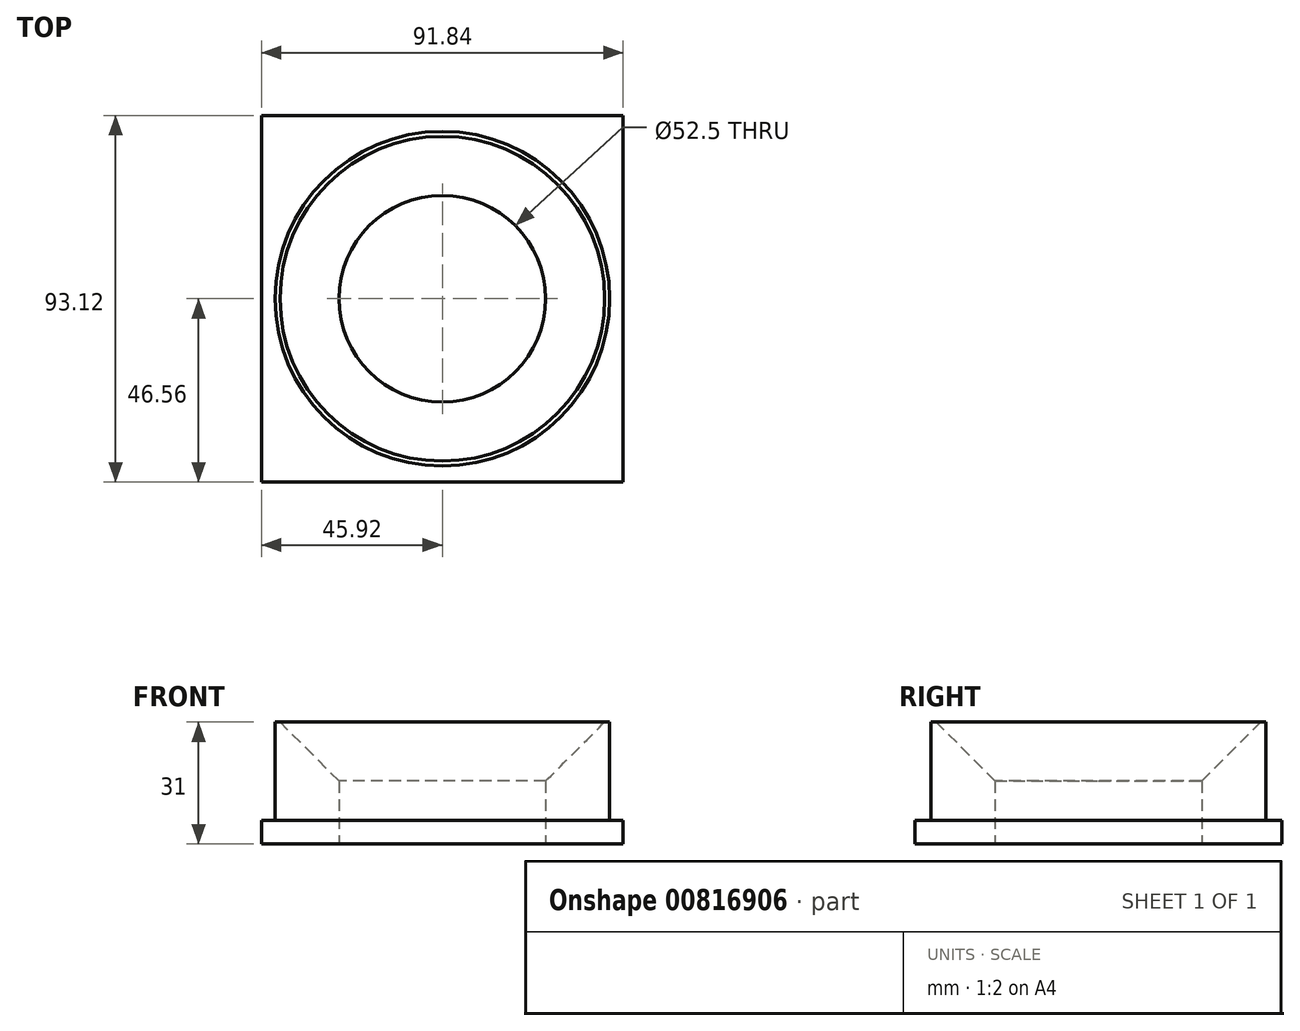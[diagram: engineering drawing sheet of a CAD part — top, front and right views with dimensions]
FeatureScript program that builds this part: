
annotation { "Feature Type Name" : "Feature", "Feature Type Description" : "" }
export const myFeature = defineFeature(function(context is Context, id is Id, definition is map)
    precondition{}
    {
        {
            var Q0;
            Q0=qCreatedBy(makeId("Top.planeOp"),FACE);
            var sketch = newSketch(context, id + "F0", { "sketchPlane" : qUnion([Q0])});
            skLineSegment(sketch, "E0.bottom", {"start": v(45.92, 46.56) * mm, "end": v(-45.92, 46.56) * mm});
            skLineSegment(sketch, "E0.top", {"start": v(45.92, -46.56) * mm, "end": v(-45.92, -46.56) * mm});
            skLineSegment(sketch, "E0.left", {"start": v(45.92, 46.56) * mm, "end": v(45.92, -46.56) * mm});
            skLineSegment(sketch, "E0.right", {"start": v(-45.92, 46.56) * mm, "end": v(-45.92, -46.56) * mm});
            skPoint(sketch, "E0.middle", {"position": v(0, 0) * mm});
            skCircle(sketch, "E1", {"center": v(0, 0) * mm, "radius": 26.25 * mm});
            skSolve(sketch);
        }
        {
            var Q0;
            Q0=makeQuery(id+"F0.imprint","IMPRINT",FACE,{"disambiguationData":[TD([[makeQuery(id+"F0.imprint","IMPRINT",EDGE,{"derivedFrom":sQuery(id+"F0.wireOp",EDGE,"E0.bottom")}),1.0]])]});
            extrude(context, id + "F1", {"entities" : qUnion([Q0]), "depth" : 6 * mm, "offsetDistance" : 25 * mm});
        }
        {
            var Q0;
            Q0=makeQuery(id+"F1.opExtrude","CAP_FACE",FACE,{"disambiguationData":[OSD([sQuery(id+"F0.wireOp",EDGE,"E0.bottom"),sQuery(id+"F0.wireOp",EDGE,"E0.top"),sQuery(id+"F0.wireOp",EDGE,"E0.left"),sQuery(id+"F0.wireOp",EDGE,"E0.right"),sQuery(id+"F0.wireOp",EDGE,"E1")])],"isStart":false});
            var sketch = newSketch(context, id + "F2", { "sketchPlane" : qUnion([Q0])});
            skCircle(sketch, "E2", {"center": v(0, 0) * mm, "radius": 42.5 * mm});
            skSolve(sketch);
        }
        {
            var Q0;
            Q0=makeQuery(id+"F2.imprint","IMPRINT",FACE,{"disambiguationData":[TD([[makeQuery(id+"F2.imprint","IMPRINT",EDGE,{"derivedFrom":sQuery(id+"F2.wireOp",EDGE,"E2")}),1.0]])]});
            extrude(context, id + "F3", {"entities" : qUnion([Q0]), "operationType" : NewBodyOperationType.ADD, "depth" : 25 * mm, "offsetDistance" : 25 * mm});
        }
        {
            var Q0;
            Q0=makeQuery(id+"F3.opExtrude","CAP_EDGE",EDGE,{"disambiguationData":[OSD([sQuery(id+"F0.wireOp",EDGE,"E1")])],"isStart":false});
            chamfer(context, id + "F4", {"entities" : qUnion([Q0]), "width" : 15 * mm, "tangentPropagation" : true});
        }
    });
